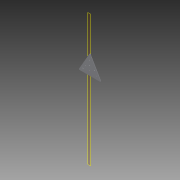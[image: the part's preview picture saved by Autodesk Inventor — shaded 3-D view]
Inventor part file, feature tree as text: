
AUTODESK INVENTOR PART (.ipt)
format: ipt  version: 2014 (Build 180170000, 170)  size: 100,352 bytes
history: native  units: in
note: dims shown in document units (in); Inventor stores cm internally (conversion verified against a paired STEP export)
features: reference x17, plane x1, extrude x1, fillet x1, sketch x1
ambient origin geometry x8: Origin, YZ Plane, XZ Plane, XY Plane, X Axis, Y Axis, Z Axis, Center Point
bodies: Solid1 (feature_tree)
feature tree (21):
  plane  "Work Plane1"
  extrude  "Extrusion1"  Depth=0.125in TaperAngle=0.0deg
  fillet  "Fillet1"  Radius=0.125in
  sketch  "Sketch1"  dims[d0=1.0in d1=0.125in d2=0.0in d3=0.125in]
  reference  "Reference1"
  reference  "Reference2"
  reference  "Reference3"
  reference  "Reference4"
  reference  "Reference5"
  reference  "Reference6"
  reference  "Reference7"
  reference  "Reference8"
  reference  "Reference9"
  reference  "Reference10"
  reference  "Reference11"
  reference  "Reference12"
  reference  "Reference13"
  reference  "Reference14"
  reference  "Reference15"
  reference  "Reference16"
  reference  "Reference17"
